# Revit family: Hager-Orion-IP66-D500-Cl.I-Inox_encl-630A-NoHosted-CH-en
name_source: partatom
category: Electrical Equipment
units: mm (PartAtom-declared; Revit-internal decimal feet)

## family parameters
Always vertical = Yes
Cut with Voids When Loaded = No
Panel Configuration = Two Columns, Circuits Across
Part Type = Panelboard
Room Calculation Point = No
Round Connector Dimension = Use Diameter
Shared = No
Work Plane-Based = Yes

## types (1)
- Surface mounted (plaster) IP66 W800 H1000 D300  - FL042BWL
    Default Elevation = 1219 mm
    EF000003 - Mounting method = EV000384 - Surface mounted (plaster)
    EF000007 - Colour = EV000154 - Other
    EF000008 - Width = 800 mm  [stored 2.62467 ft]
    EF000040 - Height = 1000 mm  [stored 3.28084 ft]
    EF000049 - Depth = 300 mm
    EF000118 - With mounting plate = No
    EF000218 - Built-in depth = 0 mm  [stored 0 ft]
    EF000266 - Number of rows = 0
    EF000339 - Type of cover = EV004216 - Door
    EF000437 - Number of conduit inlets = 0
    EF001088 - Extension possible = Yes
    EF001131 - Internal depth = 266 mm  [stored 0.872703 ft]
    EF001596 - Material housing = EV000166 - Stainless steel
    EF002950 - Width in number of modular spacings = 0
    EF003532 - Suitable for outdoor use = Yes
    EF004293 - Impact strength = EV008784 - IK10
    EF004427 - Number of modules = 0
    EF004464 - Type of door = EV002646 - Single
    EF005474 - Degree of protection (IP) = EV006422 - IP66
    EF006244 - Transparent cover/door = No
    EF006306 - With lock = No
    EF007800 - Suitable for lightning protection = No
    EF008873 - Nominal current (In) = 630 A
    EF009170 - Material plate thickness cabinet = 2 mm  [stored 0.00656168 ft]
    EF009171 - Material plate thickness door/cover = 2 mm  [stored 0.00656168 ft]
    EF009212 - Cover model = EV009916 - With notch
    EF009554 - Number of openings for flange plates = 0
    EF015940 - Cover with overpressure release = No
    HG000002 - With door or cover = Yes
    HG000003 - Range = Orion
    HG000004 - Manufacturer reference = FL042BWL
    HG000006 - Flush mounted = No
    HG000009 - Double swing door = Yes
    HG000010 - Asymmetric doors = Yes
    HG000023 - Double section enclosure = No
    HG000024 - Bottom section height = 600 mm
    HG000026 - Floor standing = No
    HG000027 - Plinth height = 0 mm  [stored 0 ft]
    Manufacturer = Hager
    Type Comments = Orion

note: [stored X ft] marks values corroborated as IEEE doubles in the binary element streams (Revit-internal decimal feet)

## geometry (parser evidence)
native form markers: Blend x4, Sweep x11
no freeform markers — native parametric forms only
